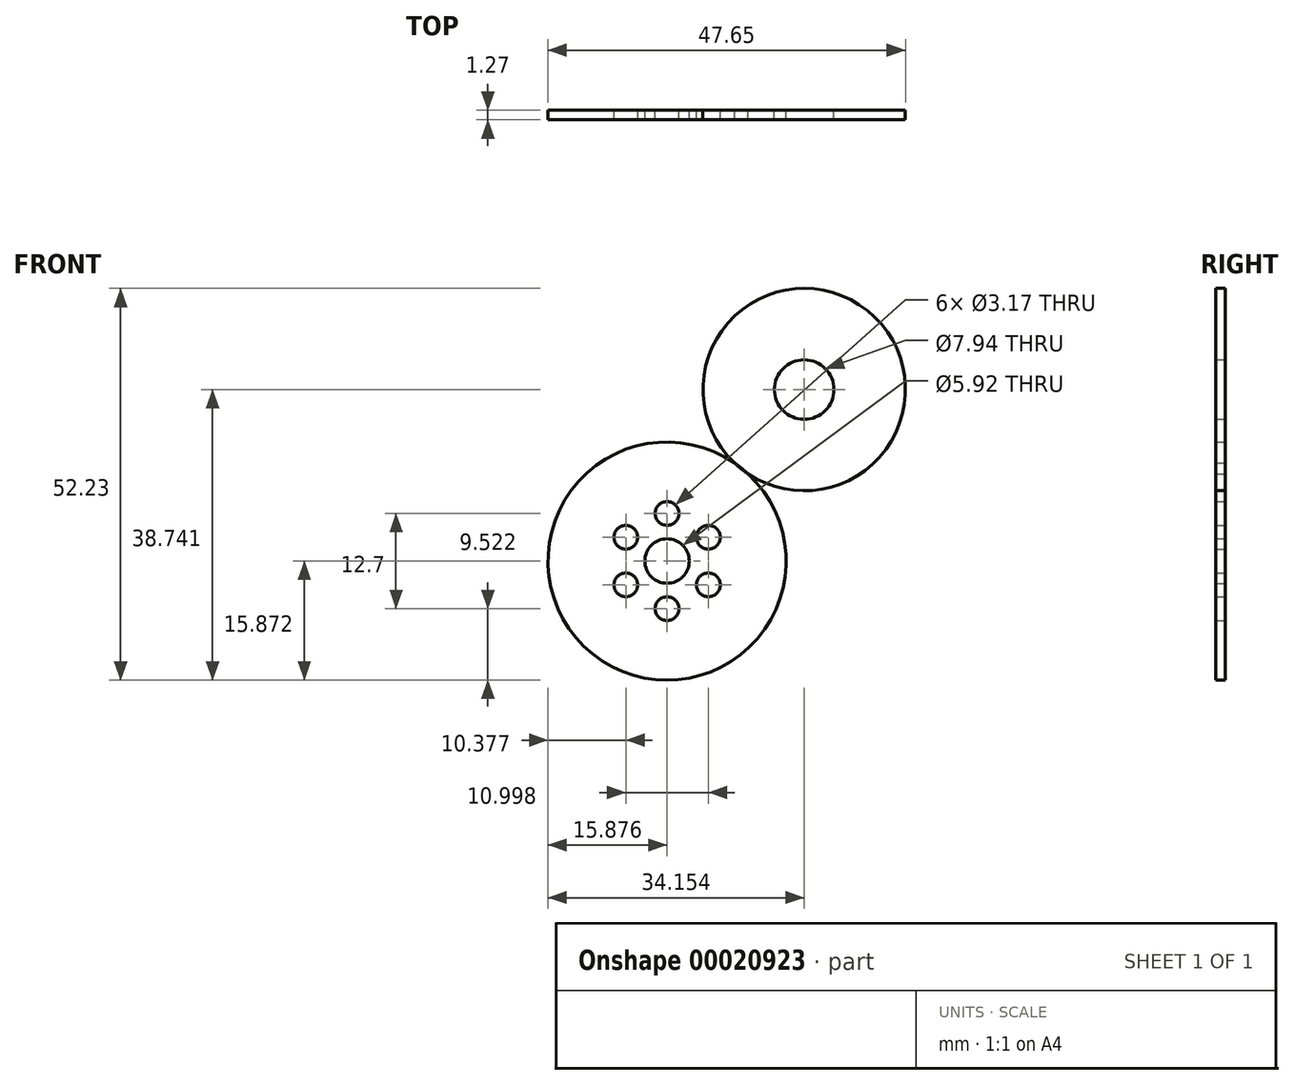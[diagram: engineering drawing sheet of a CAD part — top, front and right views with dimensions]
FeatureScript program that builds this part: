
annotation { "Feature Type Name" : "Feature", "Feature Type Description" : "" }
export const myFeature = defineFeature(function(context is Context, id is Id, definition is map)
    precondition{}
    {
        {
            var Q0;
            Q0=qCreatedBy(makeId("Front.planeOp"),FACE);
            var sketch = newSketch(context, id + "F0", { "sketchPlane" : qUnion([Q0])});
            skCircle(sketch, "E0", {"center": v(-4.87, -6.1) * mm, "radius": 15.88 * mm});
            skCircle(sketch, "E1", {"center": v(13.4, 16.77) * mm, "radius": 13.5 * mm});
            skCircle(sketch, "E2", {"center": v(-4.87, -6.1) * mm, "radius": 14.29 * mm});
            skCircle(sketch, "E3", {"center": v(13.4, 16.77) * mm, "radius": 11.9 * mm});
            skCircle(sketch, "E4", {"center": v(13.4, 16.77) * mm, "radius": 3.97 * mm});
            skCircle(sketch, "E5", {"center": v(-4.87, -6.1) * mm, "radius": 1.59 * mm});
            skCircle(sketch, "E6", {"center": v(13.4, 16.77) * mm, "radius": 1.59 * mm});
            skCircle(sketch, "E7", {"center": v(0.63, -2.92) * mm, "radius": 1.59 * mm});
            skCircle(sketch, "E8", {"center": v(-10.37, -2.92) * mm, "radius": 1.59 * mm});
            skCircle(sketch, "E9", {"center": v(-4.87, 0.25) * mm, "radius": 1.59 * mm});
            skCircle(sketch, "E10", {"center": v(-10.37, -9.27) * mm, "radius": 1.59 * mm});
            skCircle(sketch, "E11", {"center": v(-4.87, -12.45) * mm, "radius": 1.59 * mm});
            skCircle(sketch, "E12", {"center": v(0.63, -9.27) * mm, "radius": 1.59 * mm});
            skCircle(sketch, "E13", {"center": v(-4.87, -6.1) * mm, "radius": 2.96 * mm});
            skSolve(sketch);
        }
        {
            var Q0;
            Q0=makeQuery(id+"F0.imprint","IMPRINT",FACE,{"disambiguationData":[TD([[makeQuery(id+"F0.imprint","IMPRINT",EDGE,{"derivedFrom":sQuery(id+"F0.wireOp",EDGE,"E2")}),1.0]])]});
            var Q1;
            Q1=makeQuery(id+"F0.imprint","IMPRINT",FACE,{"disambiguationData":[TD([[makeQuery(id+"F0.imprint","IMPRINT",EDGE,{"derivedFrom":sQuery(id+"F0.wireOp",EDGE,"E2")}),-1.0]])]});
            var Q2;
            Q2=makeQuery(id+"F0.imprint","IMPRINT",FACE,{"disambiguationData":[TD([[makeQuery(id+"F0.imprint","IMPRINT",EDGE,{"derivedFrom":sQuery(id+"F0.wireOp",EDGE,"E3")}),1.0]])]});
            var Q3;
            Q3=makeQuery(id+"F0.imprint","IMPRINT",FACE,{"disambiguationData":[TD([[makeQuery(id+"F0.imprint","IMPRINT",EDGE,{"derivedFrom":sQuery(id+"F0.wireOp",EDGE,"E3")}),-1.0]])]});
            extrude(context, id + "F1", {"entities" : qUnion([Q0, Q1, Q2, Q3]), "depth" : 1.27 * mm});
        }
    });
